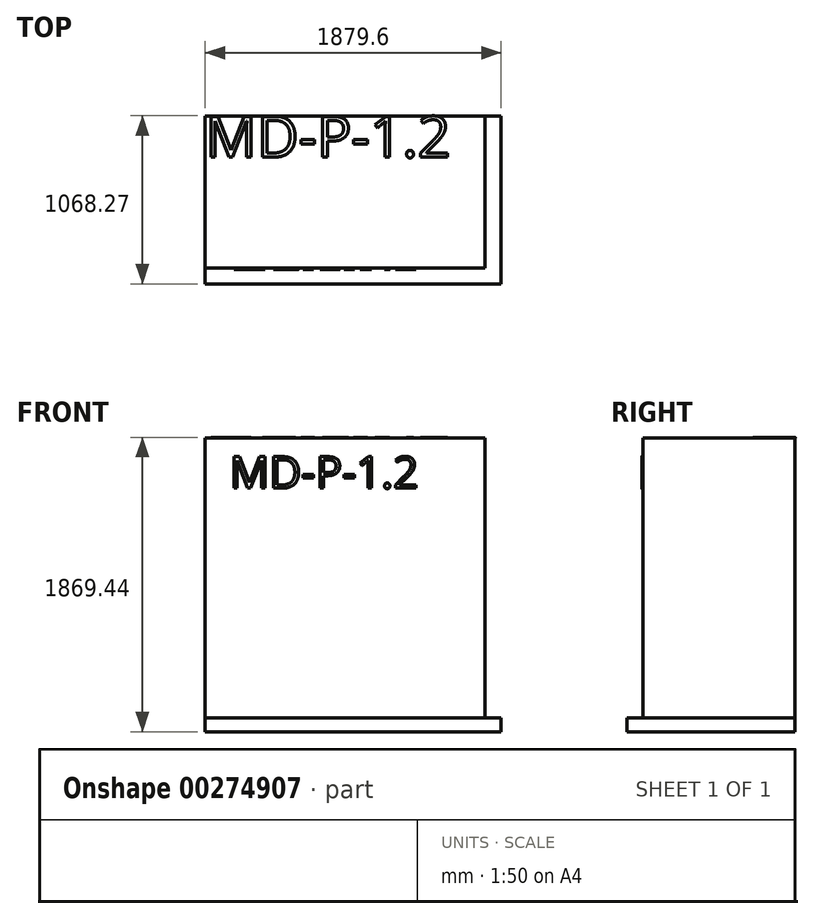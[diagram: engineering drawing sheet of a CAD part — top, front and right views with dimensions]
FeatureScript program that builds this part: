
annotation { "Feature Type Name" : "Feature", "Feature Type Description" : "" }
export const myFeature = defineFeature(function(context is Context, id is Id, definition is map)
    precondition{}
    {
        {
            var Q0;
            Q0=qCreatedBy(makeId("Top.planeOp"),FACE);
            var sketch = newSketch(context, id + "F0", { "sketchPlane" : qUnion([Q0])});
            skLineSegment(sketch, "E0.bottom", {"start": v(0, 0) * mm, "end": v(1778, 0) * mm});
            skLineSegment(sketch, "E0.top", {"start": v(0, 711.2) * mm, "end": v(1778, 711.2) * mm});
            skLineSegment(sketch, "E0.left", {"start": v(0, 0) * mm, "end": v(0, 711.2) * mm});
            skLineSegment(sketch, "E0.right", {"start": v(1778, 0) * mm, "end": v(1778, 711.2) * mm});
            skSolve(sketch);
        }
        {
            var Q0;
            Q0=makeQuery(id+"F0.imprint","IMPRINT",FACE,{"disambiguationData":[TD([[makeQuery(id+"F0.imprint","IMPRINT",EDGE,{"derivedFrom":sQuery(id+"F0.wireOp",EDGE,"E0.bottom")}),1.0]])]});
            extrude(context, id + "F1", {"entities" : qUnion([Q0]), "depth" : 1778 * mm});
        }
        {
            var Q0;
            Q0=makeQuery(id+"F1.opExtrude","SWEPT_FACE",FACE,{"disambiguationData":[OSD([sQuery(id+"F0.wireOp",EDGE,"E0.bottom")])]});
            var sketch = newSketch(context, id + "F2", { "sketchPlane" : qUnion([Q0])});
            skText(sketch, "E1", { "text": "MD-P-1.2", "fontName": "OpenSans-Regular.ttf"});
            const initialGuessF2  = {"E1": [0.15393, 1.45868, 1, 0, 0.20135]};
            skSetInitialGuess(sketch, initialGuessF2);
            skSolve(sketch);
        }
        {
            var Q0;
            Q0 = qSketchRegion(id + "F2", true);
            extrude(context, id + "F3", {"entities" : qUnion([Q0]), "operationType" : NewBodyOperationType.ADD, "depth" : 6.35 * mm});
        }
        {
            var Q0;
            {var subQ0=sQuery(id+"F0.wireOp",EDGE,"E0.left");var subQ3=sQuery(id+"F0.wireOp",EDGE,"E0.bottom");Q0=makeQuery(id+"F3.boolean.opBoolean","SPLIT",FACE,{"disambiguationData":[TD([makeQuery(id+"F1.opExtrude","SWEPT_FACE",FACE,{"disambiguationData":[OSD([subQ0])]})])],"derivedFrom":makeQuery(id+"F1.opExtrude","SWEPT_FACE",FACE,{"disambiguationData":[OSD([subQ3])]})});}
            extrude(context, id + "F4", {"entities" : qUnion([Q0]), "operationType" : NewBodyOperationType.ADD, "depth" : 254 * mm});
        }
        {
            var Q0;
            Q0=makeQuery(id+"F3.boolean.opBoolean","SPLIT",FACE,{"disambiguationData":[TD([makeQuery(id+"F3.opExtrude","SWEPT_FACE",FACE,{"disambiguationData":[OSD([sQuery(id+"F2.wireOp",EDGE,"E1.sketch_text.stroke-25")])]})])],"derivedFrom":makeQuery(id+"F1.opExtrude","SWEPT_FACE",FACE,{"disambiguationData":[OSD([sQuery(id+"F0.wireOp",EDGE,"E0.bottom")])]})});
            var Q1;
            Q1=makeQuery(id+"F3.boolean.opBoolean","SPLIT",FACE,{"disambiguationData":[TD([makeQuery(id+"F3.opExtrude","SWEPT_FACE",FACE,{"disambiguationData":[OSD([sQuery(id+"F2.wireOp",EDGE,"E1.sketch_text.stroke-44")])]})])],"derivedFrom":makeQuery(id+"F1.opExtrude","SWEPT_FACE",FACE,{"disambiguationData":[OSD([sQuery(id+"F0.wireOp",EDGE,"E0.bottom")])]})});
            extrude(context, id + "F5", {"entities" : qUnion([Q0, Q1]), "operationType" : NewBodyOperationType.ADD, "depth" : 254 * mm});
        }
        {
            var Q0;
            Q0=makeQuery(id+"F3.opExtrude","CAP_FACE",FACE,{"disambiguationData":[OSD([sQuery(id+"F2.wireOp",EDGE,"E1.sketch_text.stroke-0"),sQuery(id+"F2.wireOp",EDGE,"E1.sketch_text.stroke-1"),sQuery(id+"F2.wireOp",EDGE,"E1.sketch_text.stroke-2"),sQuery(id+"F2.wireOp",EDGE,"E1.sketch_text.stroke-3"),sQuery(id+"F2.wireOp",EDGE,"E1.sketch_text.stroke-4"),sQuery(id+"F2.wireOp",EDGE,"E1.sketch_text.stroke-5"),sQuery(id+"F2.wireOp",EDGE,"E1.sketch_text.stroke-6"),sQuery(id+"F2.wireOp",EDGE,"E1.sketch_text.stroke-7"),sQuery(id+"F2.wireOp",EDGE,"E1.sketch_text.stroke-8"),sQuery(id+"F2.wireOp",EDGE,"E1.sketch_text.stroke-9"),sQuery(id+"F2.wireOp",EDGE,"E1.sketch_text.stroke-10"),sQuery(id+"F2.wireOp",EDGE,"E1.sketch_text.stroke-11"),sQuery(id+"F2.wireOp",EDGE,"E1.sketch_text.stroke-12"),sQuery(id+"F2.wireOp",EDGE,"E1.sketch_text.stroke-13"),sQuery(id+"F2.wireOp",EDGE,"E1.sketch_text.stroke-14"),sQuery(id+"F2.wireOp",EDGE,"E1.sketch_text.stroke-15"),sQuery(id+"F2.wireOp",EDGE,"E1.sketch_text.stroke-16"),sQuery(id+"F2.wireOp",EDGE,"E1.sketch_text.stroke-17")])],"isStart":false});
            var Q1;
            Q1=makeQuery(id+"F3.opExtrude","CAP_FACE",FACE,{"disambiguationData":[OSD([sQuery(id+"F2.wireOp",EDGE,"E1.sketch_text.stroke-18"),sQuery(id+"F2.wireOp",EDGE,"E1.sketch_text.stroke-19"),sQuery(id+"F2.wireOp",EDGE,"E1.sketch_text.stroke-20"),sQuery(id+"F2.wireOp",EDGE,"E1.sketch_text.stroke-21"),sQuery(id+"F2.wireOp",EDGE,"E1.sketch_text.stroke-22"),sQuery(id+"F2.wireOp",EDGE,"E1.sketch_text.stroke-23"),sQuery(id+"F2.wireOp",EDGE,"E1.sketch_text.stroke-24"),sQuery(id+"F2.wireOp",EDGE,"E1.sketch_text.stroke-25"),sQuery(id+"F2.wireOp",EDGE,"E1.sketch_text.stroke-26"),sQuery(id+"F2.wireOp",EDGE,"E1.sketch_text.stroke-27"),sQuery(id+"F2.wireOp",EDGE,"E1.sketch_text.stroke-28"),sQuery(id+"F2.wireOp",EDGE,"E1.sketch_text.stroke-29"),sQuery(id+"F2.wireOp",EDGE,"E1.sketch_text.stroke-30"),sQuery(id+"F2.wireOp",EDGE,"E1.sketch_text.stroke-31")])],"isStart":false});
            var Q2;
            Q2=makeQuery(id+"F3.opExtrude","CAP_FACE",FACE,{"disambiguationData":[OSD([sQuery(id+"F2.wireOp",EDGE,"E1.sketch_text.stroke-36"),sQuery(id+"F2.wireOp",EDGE,"E1.sketch_text.stroke-37"),sQuery(id+"F2.wireOp",EDGE,"E1.sketch_text.stroke-38"),sQuery(id+"F2.wireOp",EDGE,"E1.sketch_text.stroke-39"),sQuery(id+"F2.wireOp",EDGE,"E1.sketch_text.stroke-40"),sQuery(id+"F2.wireOp",EDGE,"E1.sketch_text.stroke-41"),sQuery(id+"F2.wireOp",EDGE,"E1.sketch_text.stroke-42"),sQuery(id+"F2.wireOp",EDGE,"E1.sketch_text.stroke-43"),sQuery(id+"F2.wireOp",EDGE,"E1.sketch_text.stroke-44"),sQuery(id+"F2.wireOp",EDGE,"E1.sketch_text.stroke-45"),sQuery(id+"F2.wireOp",EDGE,"E1.sketch_text.stroke-46"),sQuery(id+"F2.wireOp",EDGE,"E1.sketch_text.stroke-47"),sQuery(id+"F2.wireOp",EDGE,"E1.sketch_text.stroke-48"),sQuery(id+"F2.wireOp",EDGE,"E1.sketch_text.stroke-49"),sQuery(id+"F2.wireOp",EDGE,"E1.sketch_text.stroke-50")])],"isStart":false});
            var Q3;
            Q3=makeQuery(id+"F3.opExtrude","CAP_FACE",FACE,{"disambiguationData":[OSD([sQuery(id+"F2.wireOp",EDGE,"E1.sketch_text.stroke-32"),sQuery(id+"F2.wireOp",EDGE,"E1.sketch_text.stroke-33"),sQuery(id+"F2.wireOp",EDGE,"E1.sketch_text.stroke-34"),sQuery(id+"F2.wireOp",EDGE,"E1.sketch_text.stroke-35")])],"isStart":false});
            var Q4;
            Q4=makeQuery(id+"F3.opExtrude","CAP_FACE",FACE,{"disambiguationData":[OSD([sQuery(id+"F2.wireOp",EDGE,"E1.sketch_text.stroke-51"),sQuery(id+"F2.wireOp",EDGE,"E1.sketch_text.stroke-52"),sQuery(id+"F2.wireOp",EDGE,"E1.sketch_text.stroke-53"),sQuery(id+"F2.wireOp",EDGE,"E1.sketch_text.stroke-54")])],"isStart":false});
            var Q5;
            Q5=makeQuery(id+"F3.opExtrude","CAP_FACE",FACE,{"disambiguationData":[OSD([sQuery(id+"F2.wireOp",EDGE,"E1.sketch_text.stroke-55"),sQuery(id+"F2.wireOp",EDGE,"E1.sketch_text.stroke-56"),sQuery(id+"F2.wireOp",EDGE,"E1.sketch_text.stroke-57"),sQuery(id+"F2.wireOp",EDGE,"E1.sketch_text.stroke-58"),sQuery(id+"F2.wireOp",EDGE,"E1.sketch_text.stroke-59"),sQuery(id+"F2.wireOp",EDGE,"E1.sketch_text.stroke-60"),sQuery(id+"F2.wireOp",EDGE,"E1.sketch_text.stroke-61"),sQuery(id+"F2.wireOp",EDGE,"E1.sketch_text.stroke-62"),sQuery(id+"F2.wireOp",EDGE,"E1.sketch_text.stroke-63")])],"isStart":false});
            var Q6;
            Q6=makeQuery(id+"F3.opExtrude","CAP_FACE",FACE,{"disambiguationData":[OSD([sQuery(id+"F2.wireOp",EDGE,"E1.sketch_text.stroke-64"),sQuery(id+"F2.wireOp",EDGE,"E1.sketch_text.stroke-65"),sQuery(id+"F2.wireOp",EDGE,"E1.sketch_text.stroke-66"),sQuery(id+"F2.wireOp",EDGE,"E1.sketch_text.stroke-67"),sQuery(id+"F2.wireOp",EDGE,"E1.sketch_text.stroke-68"),sQuery(id+"F2.wireOp",EDGE,"E1.sketch_text.stroke-69"),sQuery(id+"F2.wireOp",EDGE,"E1.sketch_text.stroke-70"),sQuery(id+"F2.wireOp",EDGE,"E1.sketch_text.stroke-71")])],"isStart":false});
            var Q7;
            Q7=makeQuery(id+"F3.opExtrude","CAP_FACE",FACE,{"disambiguationData":[OSD([sQuery(id+"F2.wireOp",EDGE,"E1.sketch_text.stroke-72"),sQuery(id+"F2.wireOp",EDGE,"E1.sketch_text.stroke-73"),sQuery(id+"F2.wireOp",EDGE,"E1.sketch_text.stroke-74"),sQuery(id+"F2.wireOp",EDGE,"E1.sketch_text.stroke-75"),sQuery(id+"F2.wireOp",EDGE,"E1.sketch_text.stroke-76"),sQuery(id+"F2.wireOp",EDGE,"E1.sketch_text.stroke-77"),sQuery(id+"F2.wireOp",EDGE,"E1.sketch_text.stroke-78"),sQuery(id+"F2.wireOp",EDGE,"E1.sketch_text.stroke-79"),sQuery(id+"F2.wireOp",EDGE,"E1.sketch_text.stroke-80"),sQuery(id+"F2.wireOp",EDGE,"E1.sketch_text.stroke-81"),sQuery(id+"F2.wireOp",EDGE,"E1.sketch_text.stroke-82"),sQuery(id+"F2.wireOp",EDGE,"E1.sketch_text.stroke-83"),sQuery(id+"F2.wireOp",EDGE,"E1.sketch_text.stroke-84"),sQuery(id+"F2.wireOp",EDGE,"E1.sketch_text.stroke-85"),sQuery(id+"F2.wireOp",EDGE,"E1.sketch_text.stroke-86"),sQuery(id+"F2.wireOp",EDGE,"E1.sketch_text.stroke-87"),sQuery(id+"F2.wireOp",EDGE,"E1.sketch_text.stroke-88"),sQuery(id+"F2.wireOp",EDGE,"E1.sketch_text.stroke-89"),sQuery(id+"F2.wireOp",EDGE,"E1.sketch_text.stroke-90"),sQuery(id+"F2.wireOp",EDGE,"E1.sketch_text.stroke-91")])],"isStart":false});
            extrude(context, id + "F6", {"entities" : qUnion([Q0, Q1, Q2, Q3, Q4, Q5, Q6, Q7]), "operationType" : NewBodyOperationType.ADD, "depth" : 256.54 * mm});
        }
        {
            var Q0;
            {var subQ0=sQuery(id+"F0.wireOp",EDGE,"E0.bottom");Q0=makeQuery(id+"F4.boolean.opBoolean","MERGE",FACE,{"derivedFrom":[makeQuery(id+"F1.opExtrude","CAP_FACE",FACE,{"disambiguationData":[OSD([subQ0,sQuery(id+"F0.wireOp",EDGE,"E0.top"),sQuery(id+"F0.wireOp",EDGE,"E0.left"),sQuery(id+"F0.wireOp",EDGE,"E0.right")])],"isStart":true}),makeQuery(id+"F4.opExtrude","SWEPT_FACE",FACE,{"disambiguationData":[OSD([subQ0]),TDD([makeQuery(id+"F1.opExtrude","CAP_EDGE",EDGE,{"disambiguationData":[OSD([subQ0])],"isStart":true})])]})]});}
            extrude(context, id + "F7", {"entities" : qUnion([Q0]), "operationType" : NewBodyOperationType.ADD, "depth" : 88.9 * mm});
        }
        {
            var Q0;
            {var subQ0=sQuery(id+"F0.wireOp",EDGE,"E0.bottom");Q0=makeQuery(id+"F4.boolean.opBoolean","MERGE",FACE,{"derivedFrom":[makeQuery(id+"F1.opExtrude","CAP_FACE",FACE,{"disambiguationData":[OSD([subQ0,sQuery(id+"F0.wireOp",EDGE,"E0.top"),sQuery(id+"F0.wireOp",EDGE,"E0.left"),sQuery(id+"F0.wireOp",EDGE,"E0.right")])],"isStart":false}),makeQuery(id+"F4.opExtrude","SWEPT_FACE",FACE,{"disambiguationData":[OSD([subQ0]),TDD([makeQuery(id+"F1.opExtrude","CAP_EDGE",EDGE,{"disambiguationData":[OSD([subQ0])],"isStart":false})])]})]});}
            var sketch = newSketch(context, id + "F8", { "sketchPlane" : qUnion([Q0])});
            skText(sketch, "E2", { "text": "MD-P-1.2", "fontName": "OpenSans-Regular.ttf"});
            const initialGuessF8  = {"E2": [0, 0.44983, 1, 0, 0.26137]};
            skSetInitialGuess(sketch, initialGuessF8);
            skSolve(sketch);
        }
        {
            var Q0;
            Q0 = qSketchRegion(id + "F8", true);
            extrude(context, id + "F9", {"entities" : qUnion([Q0]), "operationType" : NewBodyOperationType.ADD, "depth" : 2.54 * mm});
        }
        {
            var Q0;
            {var subQ0=sQuery(id+"F0.wireOp",EDGE,"E0.bottom");Q0=makeQuery(id+"F7.boolean.opBoolean","MERGE",FACE,{"derivedFrom":[makeQuery(id+"F4.opExtrude","CAP_FACE",FACE,{"disambiguationData":[OSD([subQ0])],"isStart":false}),makeQuery(id+"F7.opExtrude","SWEPT_FACE",FACE,{"disambiguationData":[OSD([subQ0])]})]});}
            var sketch = newSketch(context, id + "F10", { "sketchPlane" : qUnion([Q0])});
            skLineSegment(sketch, "E3.bottom", {"start": v(0, -88.9) * mm, "end": v(1778, -88.9) * mm});
            skLineSegment(sketch, "E3.top", {"start": v(0, 0) * mm, "end": v(1778, 0) * mm});
            skLineSegment(sketch, "E3.left", {"start": v(0, -88.9) * mm, "end": v(0, 0) * mm});
            skLineSegment(sketch, "E3.right", {"start": v(1778, -88.9) * mm, "end": v(1778, 0) * mm});
            skSolve(sketch);
        }
        {
            var Q0;
            Q0=makeQuery(id+"F10.imprint","IMPRINT",FACE,{"disambiguationData":[TD([[makeQuery(id+"F10.imprint","IMPRINT",EDGE,{"derivedFrom":sQuery(id+"F10.wireOp",EDGE,"E3.bottom")}),1.0]])]});
            extrude(context, id + "F11", {"entities" : qUnion([Q0]), "operationType" : NewBodyOperationType.ADD, "depth" : 101.6 * mm});
        }
        {
            var Q0;
            {var subQ0=sQuery(id+"F0.wireOp",EDGE,"E0.right");var subQ1=sQuery(id+"F0.wireOp",EDGE,"E0.bottom");Q0=makeQuery(id+"F11.boolean.opBoolean","MERGE",FACE,{"derivedFrom":[makeQuery(id+"F7.boolean.opBoolean","MERGE",FACE,{"derivedFrom":[makeQuery(id+"F4.boolean.opBoolean","MERGE",FACE,{"derivedFrom":[makeQuery(id+"F1.opExtrude","SWEPT_FACE",FACE,{"disambiguationData":[OSD([subQ0])]}),makeQuery(id+"F4.opExtrude","SWEPT_FACE",FACE,{"disambiguationData":[OSD([subQ1,subQ0])]})]}),makeQuery(id+"F7.opExtrude","SWEPT_FACE",FACE,{"disambiguationData":[OSD([subQ1,subQ0])]})]}),makeQuery(id+"F11.opExtrude","SWEPT_FACE",FACE,{"disambiguationData":[OSD([sQuery(id+"F10.wireOp",EDGE,"E3.right")])]})]});}
            var sketch = newSketch(context, id + "F12", { "sketchPlane" : qUnion([Q0])});
            skLineSegment(sketch, "E4.bottom", {"start": v(-355.6, -88.9) * mm, "end": v(711.2, -88.9) * mm});
            skLineSegment(sketch, "E4.top", {"start": v(-355.6, 0) * mm, "end": v(711.2, 0) * mm});
            skLineSegment(sketch, "E4.left", {"start": v(-355.6, -88.9) * mm, "end": v(-355.6, 0) * mm});
            skLineSegment(sketch, "E4.right", {"start": v(711.2, -88.9) * mm, "end": v(711.2, 0) * mm});
            skSolve(sketch);
        }
        {
            var Q0;
            Q0=makeQuery(id+"F12.imprint","IMPRINT",FACE,{"disambiguationData":[TD([[makeQuery(id+"F12.imprint","IMPRINT",EDGE,{"derivedFrom":sQuery(id+"F12.wireOp",EDGE,"E4.bottom")}),1.0]])]});
            extrude(context, id + "F13", {"entities" : qUnion([Q0]), "operationType" : NewBodyOperationType.ADD, "depth" : 101.6 * mm});
        }
    });
